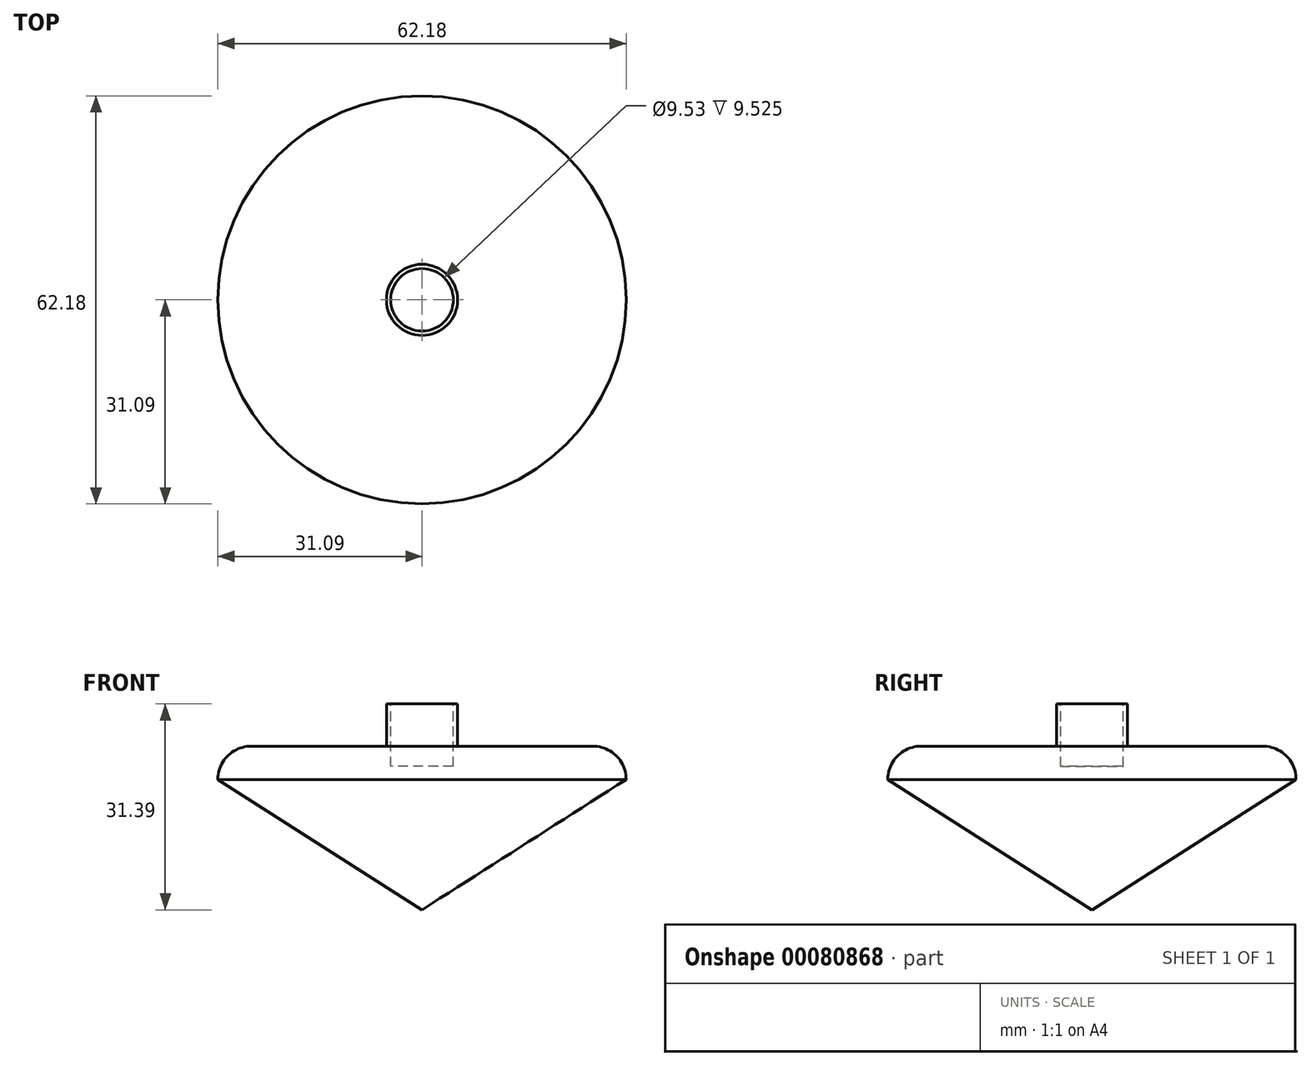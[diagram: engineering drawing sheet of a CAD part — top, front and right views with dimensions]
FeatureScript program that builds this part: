
annotation { "Feature Type Name" : "Feature", "Feature Type Description" : "" }
export const myFeature = defineFeature(function(context is Context, id is Id, definition is map)
    precondition{}
    {
        {
            var Q0;
            Q0=qCreatedBy(makeId("Front.planeOp"),FACE);
            var sketch = newSketch(context, id + "F0", { "sketchPlane" : qUnion([Q0])});
            skLineSegment(sketch, "E0", {"start": v(0, 0) * mm, "end": v(31.1, 19.88) * mm});
            skLineSegment(sketch, "E1", {"start": v(31.1, 19.88) * mm, "end": v(31.1, 24.96) * mm});
            skLineSegment(sketch, "E2", {"start": v(31.1, 24.96) * mm, "end": v(5.42, 24.96) * mm});
            skLineSegment(sketch, "E3", {"start": v(5.42, 24.96) * mm, "end": v(5.42, 31.4) * mm});
            skLineSegment(sketch, "E4", {"start": v(5.42, 31.4) * mm, "end": v(0, 31.4) * mm});
            skLineSegment(sketch, "E5", {"start": v(0, 31.4) * mm, "end": v(0, 0) * mm});
            skSolve(sketch);
        }
        {
            var Q0;
            Q0=makeQuery(id+"F0.imprint","IMPRINT",FACE,{"disambiguationData":[TD([[makeQuery(id+"F0.imprint","IMPRINT",EDGE,{"derivedFrom":sQuery(id+"F0.wireOp",EDGE,"E0")}),1.0]])]});
            var Q1;
            Q1=sQuery(id+"F0.wireOp",EDGE,"E5");
            revolve(context, id + "F1", {"entities" : qUnion([Q0]), "axis" : qUnion([Q1]), "revolveType" : RevolveType.FULL});
        }
        {
            var Q0;
            Q0=makeQuery(id+"F1.opRevolve","SWEPT_FACE",FACE,{"disambiguationData":[OSD([sQuery(id+"F0.wireOp",EDGE,"E4")])]});
            var sketch = newSketch(context, id + "F2", { "sketchPlane" : qUnion([Q0])});
            skCircle(sketch, "E6", {"center": v(0, 0) * mm, "radius": 4.76 * mm});
            skSolve(sketch);
        }
        {
            var Q0;
            Q0=makeQuery(id+"F2.imprint","IMPRINT",FACE,{"disambiguationData":[TD([[makeQuery(id+"F2.imprint","IMPRINT",EDGE,{"derivedFrom":sQuery(id+"F2.wireOp",EDGE,"E6")}),1.0]])]});
            extrude(context, id + "F3", {"entities" : qUnion([Q0]), "operationType" : NewBodyOperationType.REMOVE, "oppositeDirection" : true, "depth" : 9.52 * mm});
        }
        {
            var Q0;
            Q0=makeQuery(id+"F1.opRevolve","SWEPT_EDGE",EDGE,{"disambiguationData":[OSD([sQuery(id+"F0.wireOp",EDGE,"E1"),sQuery(id+"F0.wireOp",EDGE,"E2")])]});
            fillet(context, id + "F4", {"entities" : qUnion([Q0]), "radius" : 5.08 * mm, "tangentPropagation" : true, "allowEdgeOverflow" : false});
        }
    });
